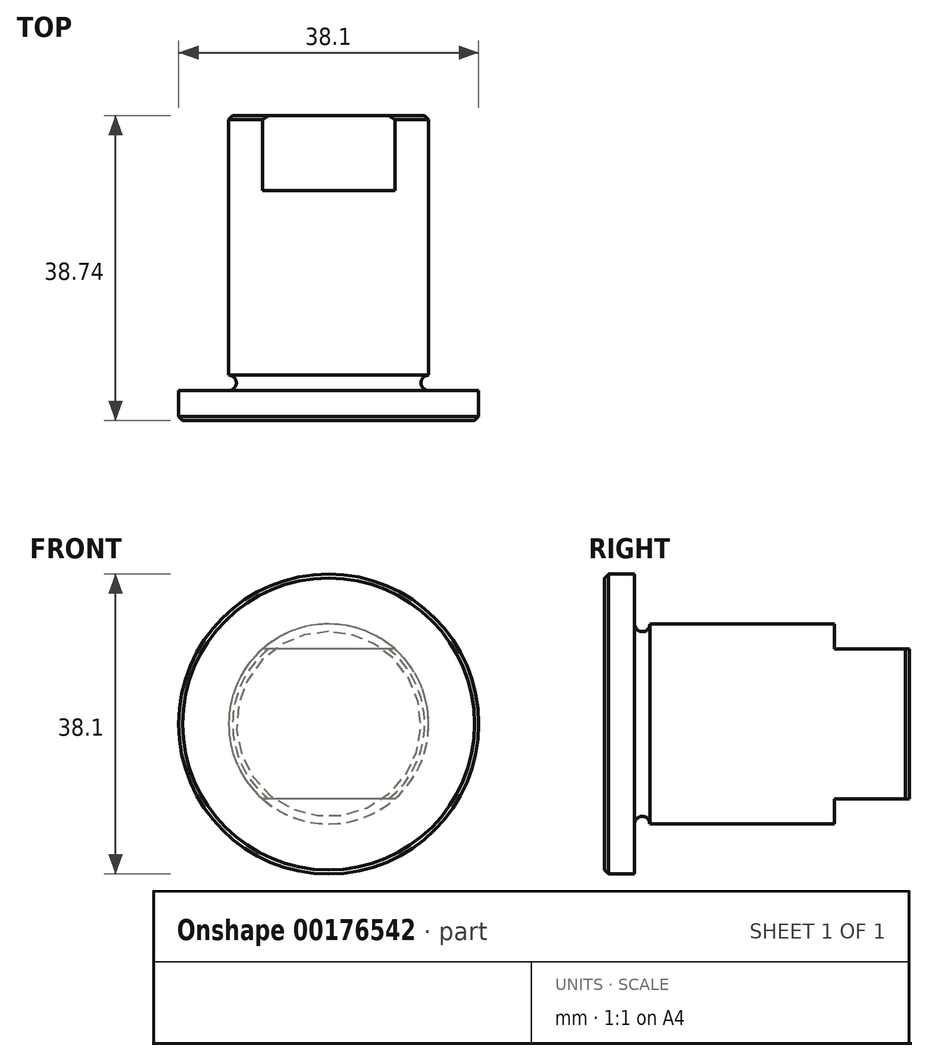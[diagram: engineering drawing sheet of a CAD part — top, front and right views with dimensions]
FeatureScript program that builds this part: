
annotation { "Feature Type Name" : "Feature", "Feature Type Description" : "" }
export const myFeature = defineFeature(function(context is Context, id is Id, definition is map)
    precondition{}
    {
        {
            var Q0;
            Q0=qCreatedBy(makeId("Top.planeOp"),FACE);
            var sketch = newSketch(context, id + "F0", { "sketchPlane" : qUnion([Q0])});
            skLineSegment(sketch, "E0.bottom", {"start": v(19.05, -1.9) * mm, "end": v(-19.05, -1.9) * mm});
            skLineSegment(sketch, "E0.top", {"start": v(19.05, 1.9) * mm, "end": v(-19.05, 1.9) * mm});
            skLineSegment(sketch, "E0.left", {"start": v(19.05, -1.9) * mm, "end": v(19.05, 1.9) * mm});
            skLineSegment(sketch, "E0.right", {"start": v(-19.05, -1.9) * mm, "end": v(-19.05, 1.9) * mm});
            skPoint(sketch, "E0.middle", {"position": v(0, 0) * mm});
            skLineSegment(sketch, "E1.bottom", {"start": v(-12.7, 1.9) * mm, "end": v(12.7, 1.9) * mm});
            skLineSegment(sketch, "E1.top", {"start": v(-12.7, 36.83) * mm, "end": v(12.7, 36.83) * mm});
            skLineSegment(sketch, "E1.left", {"start": v(-12.7, 1.9) * mm, "end": v(-12.7, 36.83) * mm});
            skLineSegment(sketch, "E1.right", {"start": v(12.7, 1.9) * mm, "end": v(12.7, 36.83) * mm});
            skLineSegment(sketch, "E2.bottom", {"start": v(9.52, -1.9) * mm, "end": v(-9.52, -1.9) * mm});
            skLineSegment(sketch, "E2.top", {"start": v(9.52, -22.48) * mm, "end": v(-9.52, -22.48) * mm});
            skLineSegment(sketch, "E2.left", {"start": v(9.52, -1.9) * mm, "end": v(9.52, -22.48) * mm});
            skLineSegment(sketch, "E2.right", {"start": v(-9.52, -1.9) * mm, "end": v(-9.52, -22.48) * mm});
            skLineSegment(sketch, "E3", {"start": v(0, 36.83) * mm, "end": v(0, -22.48) * mm});
            skArc(sketch, "E4", {"start": v(-12.7, 1.9) * mm, "mid": v(-11.73, 2.88) * mm, "end": v(-12.7, 3.85) * mm});
            skArc(sketch, "E5", {"start": v(12.7, 3.85) * mm, "mid": v(11.73, 2.88) * mm, "end": v(12.7, 1.9) * mm});
            skArc(sketch, "E6", {"start": v(-9.52, -3.85) * mm, "mid": v(-8.55, -2.88) * mm, "end": v(-9.52, -1.9) * mm});
            skArc(sketch, "E7", {"start": v(9.52, -1.9) * mm, "mid": v(8.55, -2.88) * mm, "end": v(9.53, -3.85) * mm});
            skSolve(sketch);
        }
        {
            var Q0;
            {var subQ5=sQuery(id+"F0.wireOp",EDGE,"E0.right");Q0=makeQuery(id+"F0.imprint","IMPRINT",FACE,{"disambiguationData":[TD([[makeQuery(id+"F0.imprint","IMPRINT",EDGE,{"derivedFrom":subQ5}),-1.0]])]});}
            var Q1;
            {var subQ0=sQuery(id+"F0.wireOp",EDGE,"E3");var subQ3=sQuery(id+"F0.wireOp",EDGE,"E2.bottom");var subQ4=makeQuery(id+"F0.imprint","INTERSECT",VERTEX,{"derivedFrom":[subQ3,subQ0]});Q1=makeQuery(id+"F0.imprint","IMPRINT",FACE,{"disambiguationData":[TD([[makeQuery(id+"F0.imprint","IMPRINT",EDGE,{"disambiguationData":[TD([[subQ4,-1.0]])],"derivedFrom":subQ3}),1.0]])]});}
            var Q2;
            {var subQ3=sQuery(id+"F0.wireOp",EDGE,"E4");Q2=makeQuery(id+"F0.imprint","IMPRINT",FACE,{"disambiguationData":[TD([[makeQuery(id+"F0.imprint","IMPRINT",EDGE,{"derivedFrom":subQ3}),-1.0]])]});}
            var Q3;
            Q3=sQuery(id+"F0.wireOp",EDGE,"E3");
            revolve(context, id + "F1", {"entities" : qUnion([Q0, Q1, Q2]), "axis" : qUnion([Q3]), "revolveType" : RevolveType.FULL});
        }
        {
            var Q0;
            Q0=makeQuery(id+"F1.opRevolve","SWEPT_EDGE",EDGE,{"disambiguationData":[OSD([sQuery(id+"F0.wireOp",EDGE,"E1.top"),sQuery(id+"F0.wireOp",EDGE,"E1.left")])]});
            chamfer(context, id + "F2", {"entities" : qUnion([Q0]), "width" : 0.5 * mm, "tangentPropagation" : true});
        }
        {
            var Q0;
            Q0=makeQuery(id+"F1.opRevolve","SWEPT_EDGE",EDGE,{"disambiguationData":[OSD([sQuery(id+"F0.wireOp",EDGE,"E0.bottom"),sQuery(id+"F0.wireOp",EDGE,"E0.right")])]});
            chamfer(context, id + "F3", {"entities" : qUnion([Q0]), "width" : 0.5 * mm, "tangentPropagation" : true});
        }
        {
            var Q0;
            Q0=makeQuery(id+"F1.opRevolve","SWEPT_FACE",FACE,{"disambiguationData":[OSD([sQuery(id+"F0.wireOp",EDGE,"E1.top")])]});
            var sketch = newSketch(context, id + "F4", { "sketchPlane" : qUnion([Q0])});
            skLineSegment(sketch, "E8.bottom", {"start": v(12.7, -12.7) * mm, "end": v(-12.7, -12.7) * mm});
            skLineSegment(sketch, "E8.top", {"start": v(12.7, 12.7) * mm, "end": v(-12.7, 12.7) * mm});
            skLineSegment(sketch, "E8.left", {"start": v(12.7, -12.7) * mm, "end": v(12.7, 12.7) * mm});
            skLineSegment(sketch, "E8.right", {"start": v(-12.7, -12.7) * mm, "end": v(-12.7, 12.7) * mm});
            skPoint(sketch, "E8.middle", {"position": v(0, 0) * mm});
            skLineSegment(sketch, "E9", {"start": v(-12.7, 9.53) * mm, "end": v(12.7, 9.53) * mm});
            skLineSegment(sketch, "E10", {"start": v(-12.7, -9.53) * mm, "end": v(12.7, -9.53) * mm});
            skSolve(sketch);
        }
        {
            var Q0;
            {var subQ0=sQuery(id+"F4.wireOp",EDGE,"E9");var subQ1=sQuery(id+"F0.wireOp",EDGE,"E1.top");var subQ2=makeQuery(id+"F2.opChamfer","BLEND_EDGE",EDGE,{"blendedFrom":[makeQuery(id+"F1.opRevolve","SWEPT_EDGE",EDGE,{"disambiguationData":[OSD([subQ1,sQuery(id+"F0.wireOp",EDGE,"E1.left")])]}),makeQuery(id+"F1.opRevolve","SWEPT_FACE",FACE,{"disambiguationData":[OSD([subQ1])]})],"blendedInto":[makeQuery(id+"F1.opRevolve","SWEPT_FACE",FACE,{"disambiguationData":[OSD([subQ1])]})]});var subQ3=makeQuery(id+"F4.imprint","INTERSECT",VERTEX,{"disambiguationData":[OD(0.0)],"derivedFrom":[subQ2,subQ0]});Q0=makeQuery(id+"F4.imprint","IMPRINT",FACE,{"disambiguationData":[TD([[makeQuery(id+"F4.imprint","IMPRINT",EDGE,{"disambiguationData":[TD([[subQ3,-1.0]])],"derivedFrom":subQ0}),1.0]])]});}
            var Q1;
            {var subQ6=sQuery(id+"F4.wireOp",EDGE,"E8.top");Q1=makeQuery(id+"F4.imprint","IMPRINT",FACE,{"disambiguationData":[TD([[makeQuery(id+"F4.imprint","IMPRINT",EDGE,{"derivedFrom":subQ6}),1.0]])]});}
            var Q2;
            {var subQ1=sQuery(id+"F4.wireOp",EDGE,"E8.bottom");Q2=makeQuery(id+"F4.imprint","IMPRINT",FACE,{"disambiguationData":[TD([[makeQuery(id+"F4.imprint","IMPRINT",EDGE,{"derivedFrom":subQ1}),-1.0]])]});}
            var Q3;
            {var subQ0=sQuery(id+"F4.wireOp",EDGE,"E10");var subQ1=sQuery(id+"F0.wireOp",EDGE,"E1.top");var subQ2=makeQuery(id+"F2.opChamfer","BLEND_EDGE",EDGE,{"blendedFrom":[makeQuery(id+"F1.opRevolve","SWEPT_EDGE",EDGE,{"disambiguationData":[OSD([subQ1,sQuery(id+"F0.wireOp",EDGE,"E1.left")])]}),makeQuery(id+"F1.opRevolve","SWEPT_FACE",FACE,{"disambiguationData":[OSD([subQ1])]})],"blendedInto":[makeQuery(id+"F1.opRevolve","SWEPT_FACE",FACE,{"disambiguationData":[OSD([subQ1])]})]});var subQ3=makeQuery(id+"F4.imprint","INTERSECT",VERTEX,{"disambiguationData":[OD(0.0)],"derivedFrom":[subQ2,subQ0]});Q3=makeQuery(id+"F4.imprint","IMPRINT",FACE,{"disambiguationData":[TD([[makeQuery(id+"F4.imprint","IMPRINT",EDGE,{"disambiguationData":[TD([[subQ3,-1.0]])],"derivedFrom":subQ0}),-1.0]])]});}
            extrude(context, id + "F5", {"entities" : qUnion([Q0, Q1, Q2, Q3]), "operationType" : NewBodyOperationType.REMOVE, "oppositeDirection" : true, "depth" : 9.52 * mm});
        }
    });
